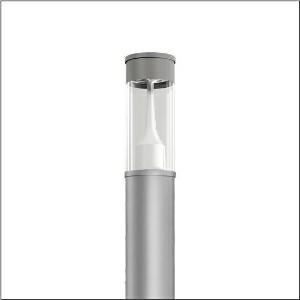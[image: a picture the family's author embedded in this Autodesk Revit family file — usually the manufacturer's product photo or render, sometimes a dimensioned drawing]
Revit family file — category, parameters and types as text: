
# Revit family: city-light_260_iq___pl1_2s_5xa5295jf14h_6623
name_source: partatom
category: Lighting Fixtures
units: mm (PartAtom-declared; Revit-internal decimal feet)

## family parameters
Cut with Voids When Loaded = No
Host = Face
Light Source = No
Part Type = Normal
Room Calculation Point = No
Round Connector Dimension = Use Diameter
Shared = No

## types (1)
- --- (1 x LED, 2970 lm, 19.3 W, 3000K)
    Apparent Load = 19 VA
    CIE Flux Codes = 23 62 94 96 100
    Color Rendering = 70
    Color Temperature = 3000K
    Default Elevation = 1800 mm
    Description = City-Light 260 iQ, light pillar, Module 540 iQ-SR, primary light control with 3 zone facetted reflector, of plastic, silver coated, highly specular, structured, primary optical cover: cover, of PMMA, transparent, light distribution: PL1.2s, primary light characteristic: symmetric, LED, High Power LED, rated luminous flux: 2.970lm, luminous efficacy: 154lm/W, light colour: 730, colour temperature: 3000K, control gear: iQ Street-Remote, control: Auto-Match, Temp-Guard, Lumen-Switch, Night-Set, Smart-Wire, Light-Fading, Desk-Remote (wireless, voltage-free reading and setting of iQ features in the workshop via application-optimized NFC function/RFID function), optimised constant luminous flux control (CLO 2.0), Street-Remote, pre-setting: logarithmic dimming characteristic, with terminal, 6-pole, max. 2.5mm², mains connection: 230..240V, AC, 50/60Hz, start of lifetime: 19W, end of service life: 21W, reduction: 10W, luminaire housing, cylindrical, of extruded aluminium section, coated, Siteco® metallic grey (DB 702S), length: 2.600mm, diameter: 200mm, Module 540 iQ-SR, traffic white (RAL 9016), equipment: standard, protection rating (complete): IP65, insulation class (complete): insulation class II (safety insulation), certification: CE, ENEC, VDE, packaging unit: 1 piece

Light Distribution: PL1.2s
    Height = 500 mm
    Lamp = 1 x LED
    Lamp Light Flux = 2970 lm
    Lamp Power = 19.3 W
    Lamp count = 1
    Length = 200 mm  [stored 0.656168 ft]
    Luminous efficacy = 154 lm/W
    Manufacturer = Siteco
    ModVariant = No
    Model = 5XA5295JF14H
    Mounting Place = Floor
    Mounting Type = Freestanding
    Number of Poles = 1
    OnlyDefault = Yes
    Power Factor = 1
    Product Name = City-Light 260 iQ | PL1.2s
    Product group = light pillar
    ProductGroupID = 1301
    Protection Class = Protection class II
    Protection Degree = IP 65
    RLX_Detail_Level = 1
    RLX_Emergency_Light_Flux = 0 lm
    RLX_Emergency_Type = 0
    RLX_Emergency_Type_DB = No
    RlxData = <blob elided: 28713 chars, md5=c88bbaf5>
    Socket = socket
    Standby Power = 0 W
    System Light Flux = 2970 lm
    System Power = 19 W
    Type Comments = factory setting: luminous flux: 100 % | dim-lin: 254 | 403 mA
    Type Image = l_1006920.jpg
    URL = http://relux.com
    VarID = @adj_039701
    Voltage = 0 V
    Weight = 0.00 kg
    Width = 0 mm  [stored 0 ft]

note: [stored X ft] marks values corroborated as IEEE doubles in the binary element streams (Revit-internal decimal feet)

## geometry (parser evidence)
native form markers: Blend x4, Sweep x10
no freeform markers — native parametric forms only
